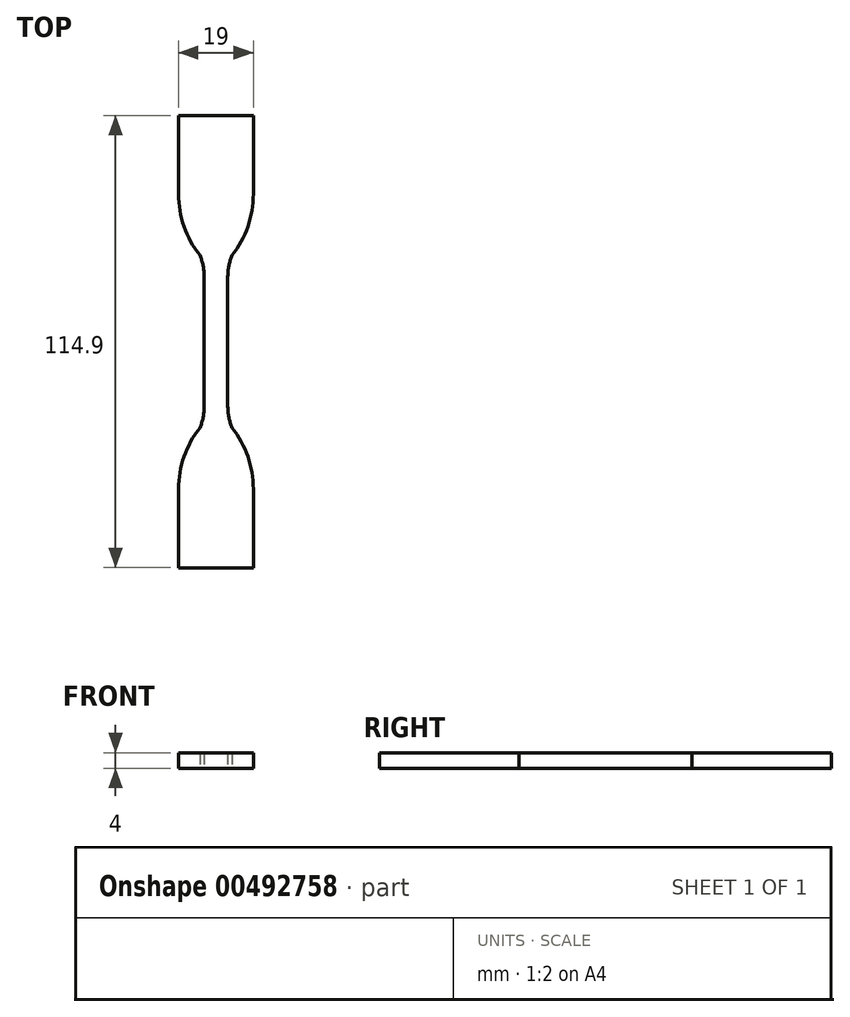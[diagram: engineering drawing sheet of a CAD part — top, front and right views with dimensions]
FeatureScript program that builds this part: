
annotation { "Feature Type Name" : "Feature", "Feature Type Description" : "" }
export const myFeature = defineFeature(function(context is Context, id is Id, definition is map)
    precondition{}
    {
        {
            var Q0;
            Q0=qCreatedBy(makeId("Top.planeOp"),FACE);
            var sketch = newSketch(context, id + "F0", { "sketchPlane" : qUnion([Q0])});
            skLineSegment(sketch, "E0", {"start": v(-3, 0) * mm, "end": v(-3, 0) * mm});
            skLineSegment(sketch, "E1", {"start": v(-9.5, 37.45) * mm, "end": v(-9.5, 57.45) * mm});
            skLineSegment(sketch, "E2", {"start": v(-9.5, 57.45) * mm, "end": v(0, 57.45) * mm});
            skLineSegment(sketch, "E3", {"start": v(0, 57.45) * mm, "end": v(0, 0) * mm});
            skLineSegment(sketch, "E4", {"start": v(0, 0) * mm, "end": v(-3, 0) * mm});
            skArc(sketch, "E5", {"start": v(-3, 16.5) * mm, "mid": v(-3.28, 19.27) * mm, "end": v(-4.1, 21.93) * mm});
            skArc(sketch, "E6", {"start": v(-9.5, 37.45) * mm, "mid": v(-8.11, 29.24) * mm, "end": v(-4.1, 21.93) * mm});
            skLineSegment(sketch, "E7", {"start": v(-3, 0) * mm, "end": v(-3, 16.5) * mm});
            skSolve(sketch);
        }
        {
            var Q0;
            Q0 = qSketchRegion(id + "F0", true);
            extrude(context, id + "F1", {"entities" : qUnion([Q0]), "depth" : 4 * mm});
        }
        {
            var Q0;
            Q0=makeQuery(id+"F1.opExtrude","SWEPT_BODY",BODY,{"disambiguationData":[OSD([sQuery(id+"F0.wireOp",EDGE,"E1"),sQuery(id+"F0.wireOp",EDGE,"E2"),sQuery(id+"F0.wireOp",EDGE,"E3"),sQuery(id+"F0.wireOp",EDGE,"E4"),sQuery(id+"F0.wireOp",EDGE,"E5"),sQuery(id+"F0.wireOp",EDGE,"E6"),sQuery(id+"F0.wireOp",EDGE,"E7")])]});
            var Q1;
            Q1=makeQuery(id+"F1.opExtrude","SWEPT_FACE",FACE,{"disambiguationData":[OSD([sQuery(id+"F0.wireOp",EDGE,"E4")])]});
            mirror(context, id + "F2", {"operationType" : NewBodyOperationType.ADD, "entities" : qUnion([Q0]), "mirrorPlane" : qUnion([Q1])});
        }
        {
            var Q0;
            Q0=makeQuery(id+"F1.opExtrude","SWEPT_BODY",BODY,{"disambiguationData":[OSD([sQuery(id+"F0.wireOp",EDGE,"E1"),sQuery(id+"F0.wireOp",EDGE,"E2"),sQuery(id+"F0.wireOp",EDGE,"E3"),sQuery(id+"F0.wireOp",EDGE,"E4"),sQuery(id+"F0.wireOp",EDGE,"E5"),sQuery(id+"F0.wireOp",EDGE,"E6"),sQuery(id+"F0.wireOp",EDGE,"E7")])]});
            var Q1;
            {var subQ0=makeQuery(id+"F1.opExtrude","SWEPT_FACE",FACE,{"disambiguationData":[OSD([sQuery(id+"F0.wireOp",EDGE,"E3")])]});Q1=makeQuery(id+"F2.boolean.opBoolean","MERGE",FACE,{"derivedFrom":[subQ0,makeQuery(id+"F2.opPattern","COPY",FACE,{"derivedFrom":subQ0,"instanceName":"1"})]});}
            mirror(context, id + "F3", {"operationType" : NewBodyOperationType.ADD, "entities" : qUnion([Q0]), "mirrorPlane" : qUnion([Q1])});
        }
    });
